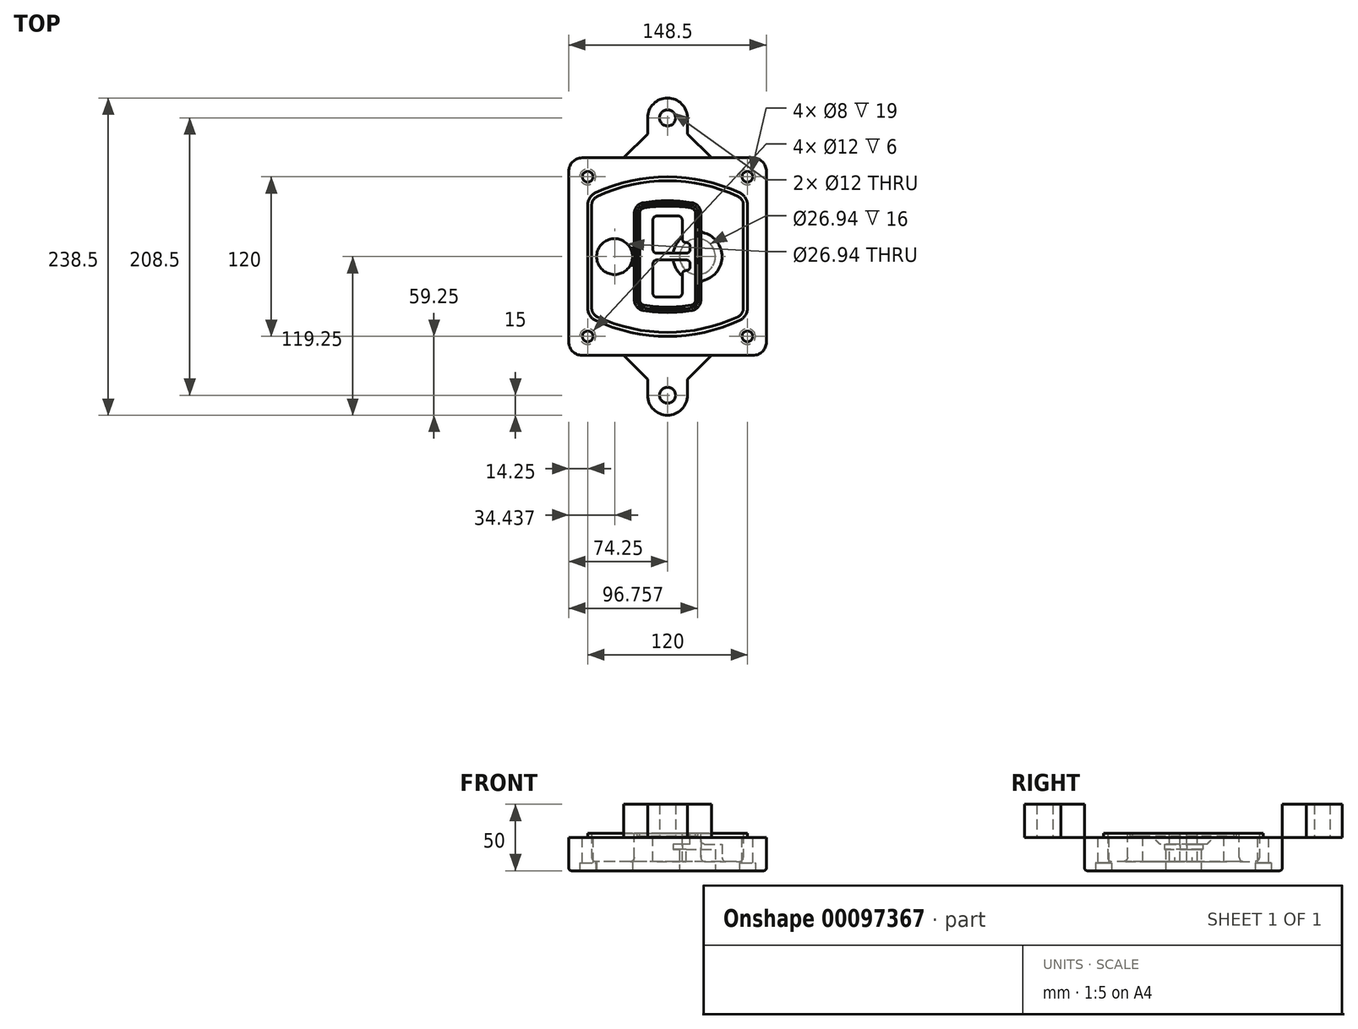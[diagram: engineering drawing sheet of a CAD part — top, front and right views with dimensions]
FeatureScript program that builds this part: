
annotation { "Feature Type Name" : "Feature", "Feature Type Description" : "" }
export const myFeature = defineFeature(function(context is Context, id is Id, definition is map)
    precondition{}
    {
        {
            var Q0;
            Q0=qCreatedBy(makeId("Top.planeOp"),FACE);
            var sketch = newSketch(context, id + "F0", { "sketchPlane" : qUnion([Q0])});
            skPoint(sketch, "E0.rect.middle", {"position": v(0, 0) * mm});
            skLineSegment(sketch, "E1.bottom", {"start": v(-64.25, -74.25) * mm, "end": v(64.25, -74.25) * mm});
            skLineSegment(sketch, "E1.top", {"start": v(-64.25, 74.25) * mm, "end": v(64.25, 74.25) * mm});
            skLineSegment(sketch, "E1.left", {"start": v(-74.25, -64.25) * mm, "end": v(-74.25, 64.25) * mm});
            skLineSegment(sketch, "E1.right", {"start": v(74.25, -64.25) * mm, "end": v(74.25, 64.25) * mm});
            skLineSegment(sketch, "E2", {"start": v(-74.25, 74.25) * mm, "end": v(74.25, -74.25) * mm, "construction": true});
            skLineSegment(sketch, "E3", {"start": v(74.25, 74.25) * mm, "end": v(-74.25, -74.25) * mm, "construction": true});
            skCircle(sketch, "E4", {"center": v(-60, 60) * mm, "radius": 4 * mm});
            skCircle(sketch, "E5", {"center": v(60, 60) * mm, "radius": 4 * mm});
            skCircle(sketch, "E6", {"center": v(60, -60) * mm, "radius": 4 * mm});
            skCircle(sketch, "E7", {"center": v(-60, -60) * mm, "radius": 4 * mm});
            skLineSegment(sketch, "E8", {"start": v(-60, 60) * mm, "end": v(60, 60) * mm, "construction": true});
            skLineSegment(sketch, "E9", {"start": v(60, 60) * mm, "end": v(60, -60) * mm, "construction": true});
            skLineSegment(sketch, "E10", {"start": v(60, -60) * mm, "end": v(-60, -60) * mm, "construction": true});
            skLineSegment(sketch, "E11", {"start": v(-60, -60) * mm, "end": v(-60, 60) * mm, "construction": true});
            skLineSegment(sketch, "E12", {"start": v(-60, 38.83) * mm, "end": v(-60, -38.83) * mm});
            skLineSegment(sketch, "E13", {"start": v(60, 38.83) * mm, "end": v(60, -38.83) * mm});
            skArc(sketch, "E14", {"start": v(54.26, 47.88) * mm, "mid": v(0, 60) * mm, "end": v(-54.26, 47.88) * mm});
            skArc(sketch, "E15", {"start": v(-54.26, -47.88) * mm, "mid": v(0, -60) * mm, "end": v(54.26, -47.88) * mm});
            skLineSegment(sketch, "E16", {"start": v(-60, 0) * mm, "end": v(60, 0) * mm, "construction": true});
            skPoint(sketch, "E17.visualSharp", {"position": v(-60, -45) * mm});
            skArc(sketch, "E17.filletArc", {"start": v(-60, -38.83) * mm, "mid": v(-58.44, -44.2) * mm, "end": v(-54.26, -47.88) * mm});
            skPoint(sketch, "E18.visualSharp", {"position": v(-60, 45) * mm});
            skArc(sketch, "E18.filletArc", {"start": v(-54.26, 47.88) * mm, "mid": v(-58.44, 44.2) * mm, "end": v(-60, 38.83) * mm});
            skPoint(sketch, "E19.visualSharp", {"position": v(60, 45) * mm});
            skArc(sketch, "E19.filletArc", {"start": v(60, 38.83) * mm, "mid": v(58.44, 44.2) * mm, "end": v(54.26, 47.88) * mm});
            skPoint(sketch, "E20.visualSharp", {"position": v(60, -45) * mm});
            skArc(sketch, "E20.filletArc", {"start": v(54.26, -47.88) * mm, "mid": v(58.44, -44.2) * mm, "end": v(60, -38.83) * mm});
            skPoint(sketch, "E21.visualSharp", {"position": v(-74.25, 74.25) * mm});
            skArc(sketch, "E21.filletArc", {"start": v(-64.25, 74.25) * mm, "mid": v(-71.32, 71.32) * mm, "end": v(-74.25, 64.25) * mm});
            skPoint(sketch, "E22.visualSharp", {"position": v(74.25, 74.25) * mm});
            skArc(sketch, "E22.filletArc", {"start": v(74.25, 64.25) * mm, "mid": v(71.32, 71.32) * mm, "end": v(64.25, 74.25) * mm});
            skPoint(sketch, "E23.visualSharp", {"position": v(74.25, -74.25) * mm});
            skArc(sketch, "E23.filletArc", {"start": v(64.25, -74.25) * mm, "mid": v(71.32, -71.32) * mm, "end": v(74.25, -64.25) * mm});
            skPoint(sketch, "E24.visualSharp", {"position": v(-74.25, -74.25) * mm});
            skArc(sketch, "E24.filletArc", {"start": v(-74.25, -64.25) * mm, "mid": v(-71.32, -71.32) * mm, "end": v(-64.25, -74.25) * mm});
            skArc(sketch, "E25.0", {"start": v(57, 38.83) * mm, "mid": v(55.9, 42.58) * mm, "end": v(52.98, 45.17) * mm});
            skLineSegment(sketch, "E25.1", {"start": v(57, 38.83) * mm, "end": v(57, -38.83) * mm});
            skArc(sketch, "E25.2", {"start": v(52.98, -45.17) * mm, "mid": v(55.9, -42.58) * mm, "end": v(57, -38.83) * mm});
            skArc(sketch, "E25.3", {"start": v(-52.98, -45.17) * mm, "mid": v(0, -57) * mm, "end": v(52.98, -45.17) * mm});
            skArc(sketch, "E25.4", {"start": v(-57, -38.83) * mm, "mid": v(-55.9, -42.58) * mm, "end": v(-52.98, -45.17) * mm});
            skArc(sketch, "E25.5", {"start": v(52.98, 45.17) * mm, "mid": v(0, 57) * mm, "end": v(-52.98, 45.17) * mm});
            skLineSegment(sketch, "E25.6", {"start": v(-57, 38.83) * mm, "end": v(-57, -38.83) * mm});
            skArc(sketch, "E25.7", {"start": v(-52.98, 45.17) * mm, "mid": v(-55.9, 42.58) * mm, "end": v(-57, 38.83) * mm});
            skArc(sketch, "E26.0", {"start": v(-55.96, 51.5) * mm, "mid": v(-61.82, 46.33) * mm, "end": v(-64, 38.83) * mm});
            skArc(sketch, "E26.1", {"start": v(55.96, 51.5) * mm, "mid": v(0, 64) * mm, "end": v(-55.96, 51.5) * mm});
            skArc(sketch, "E26.2", {"start": v(64, 38.83) * mm, "mid": v(61.82, 46.33) * mm, "end": v(55.96, 51.5) * mm});
            skLineSegment(sketch, "E26.3", {"start": v(64, 38.83) * mm, "end": v(64, -38.83) * mm});
            skArc(sketch, "E26.4", {"start": v(55.96, -51.5) * mm, "mid": v(61.82, -46.33) * mm, "end": v(64, -38.83) * mm});
            skLineSegment(sketch, "E26.5", {"start": v(-64, 38.83) * mm, "end": v(-64, -38.83) * mm});
            skArc(sketch, "E26.6", {"start": v(-55.96, -51.5) * mm, "mid": v(0, -64) * mm, "end": v(55.96, -51.5) * mm});
            skArc(sketch, "E26.7", {"start": v(-64, -38.83) * mm, "mid": v(-61.82, -46.33) * mm, "end": v(-55.96, -51.5) * mm});
            skSolve(sketch);
        }
        {
            var Q0;
            Q0=makeQuery(id+"F0.imprint","IMPRINT",FACE,{"disambiguationData":[TD([[makeQuery(id+"F0.imprint","IMPRINT",EDGE,{"derivedFrom":sQuery(id+"F0.wireOp",EDGE,"E1.bottom")}),1.0]])]});
            var Q1;
            Q1=makeQuery(id+"F0.imprint","IMPRINT",FACE,{"disambiguationData":[TD([[makeQuery(id+"F0.imprint","IMPRINT",EDGE,{"derivedFrom":sQuery(id+"F0.wireOp",EDGE,"E12")}),1.0]])]});
            var Q2;
            Q2=makeQuery(id+"F0.imprint","IMPRINT",FACE,{"disambiguationData":[TD([[makeQuery(id+"F0.imprint","IMPRINT",EDGE,{"derivedFrom":sQuery(id+"F0.wireOp",EDGE,"E25.0")}),1.0]])]});
            var Q3;
            Q3=makeQuery(id+"F0.imprint","IMPRINT",FACE,{"disambiguationData":[TD([[makeQuery(id+"F0.imprint","IMPRINT",EDGE,{"derivedFrom":sQuery(id+"F0.wireOp",EDGE,"E12")}),-1.0]])]});
            extrude(context, id + "F1", {"entities" : qUnion([Q0, Q1, Q2, Q3]), "oppositeDirection" : true, "depth" : 25 * mm});
        }
        {
            var Q0;
            Q0=makeQuery(id+"F0.imprint","IMPRINT",FACE,{"disambiguationData":[TD([[makeQuery(id+"F0.imprint","IMPRINT",EDGE,{"derivedFrom":sQuery(id+"F0.wireOp",EDGE,"E12")}),1.0]])]});
            extrude(context, id + "F2", {"entities" : qUnion([Q0]), "operationType" : NewBodyOperationType.ADD, "depth" : 3 * mm});
        }
        {
            var Q0;
            Q0=makeQuery(id+"F0.imprint","IMPRINT",FACE,{"disambiguationData":[TD([[makeQuery(id+"F0.imprint","IMPRINT",EDGE,{"derivedFrom":sQuery(id+"F0.wireOp",EDGE,"E25.0")}),1.0]])]});
            extrude(context, id + "F3", {"entities" : qUnion([Q0]), "operationType" : NewBodyOperationType.REMOVE, "oppositeDirection" : true, "depth" : 18 * mm});
        }
        {
            var Q0;
            Q0=makeQuery(id+"F2.opExtrude","CAP_FACE",FACE,{"disambiguationData":[OSD([sQuery(id+"F0.wireOp",EDGE,"E12"),sQuery(id+"F0.wireOp",EDGE,"E13"),sQuery(id+"F0.wireOp",EDGE,"E14"),sQuery(id+"F0.wireOp",EDGE,"E15"),sQuery(id+"F0.wireOp",EDGE,"E17.filletArc"),sQuery(id+"F0.wireOp",EDGE,"E18.filletArc"),sQuery(id+"F0.wireOp",EDGE,"E19.filletArc"),sQuery(id+"F0.wireOp",EDGE,"E20.filletArc"),sQuery(id+"F0.wireOp",EDGE,"E25.0"),sQuery(id+"F0.wireOp",EDGE,"E25.1"),sQuery(id+"F0.wireOp",EDGE,"E25.2"),sQuery(id+"F0.wireOp",EDGE,"E25.3"),sQuery(id+"F0.wireOp",EDGE,"E25.4"),sQuery(id+"F0.wireOp",EDGE,"E25.5"),sQuery(id+"F0.wireOp",EDGE,"E25.6"),sQuery(id+"F0.wireOp",EDGE,"E25.7")])],"isStart":false});
            var sketch = newSketch(context, id + "F4", { "sketchPlane" : qUnion([Q0])});
            skArc(sketch, "E27.0", {"start": v(-18.34, -40.45) * mm, "mid": v(0, -42) * mm, "end": v(18.34, -40.45) * mm});
            skArc(sketch, "E28.0", {"start": v(18.34, 40.45) * mm, "mid": v(0, 42) * mm, "end": v(-18.34, 40.45) * mm});
            skLineSegment(sketch, "E29", {"start": v(-25, 32.57) * mm, "end": v(-25, -32.57) * mm});
            skLineSegment(sketch, "E30", {"start": v(25, 32.57) * mm, "end": v(25, -32.57) * mm});
            skLineSegment(sketch, "E31", {"start": v(-25, 39.1) * mm, "end": v(25, 39.1) * mm, "construction": true});
            skLineSegment(sketch, "E32", {"start": v(-25, -39.1) * mm, "end": v(25, -39.1) * mm, "construction": true});
            skPoint(sketch, "E33.visualSharp", {"position": v(-25, 39.1) * mm});
            skArc(sketch, "E33.filletArc", {"start": v(-18.34, 40.45) * mm, "mid": v(-23.11, 37.73) * mm, "end": v(-25, 32.57) * mm});
            skPoint(sketch, "E34.visualSharp", {"position": v(25, 39.1) * mm});
            skArc(sketch, "E34.filletArc", {"start": v(25, 32.57) * mm, "mid": v(23.11, 37.73) * mm, "end": v(18.34, 40.45) * mm});
            skPoint(sketch, "E35.visualSharp", {"position": v(25, -39.1) * mm});
            skArc(sketch, "E35.filletArc", {"start": v(18.34, -40.45) * mm, "mid": v(23.11, -37.73) * mm, "end": v(25, -32.57) * mm});
            skPoint(sketch, "E36.visualSharp", {"position": v(-25, -39.1) * mm});
            skArc(sketch, "E36.filletArc", {"start": v(-25, -32.57) * mm, "mid": v(-23.11, -37.73) * mm, "end": v(-18.34, -40.45) * mm});
            skArc(sketch, "E37.0", {"start": v(52.98, 45.17) * mm, "mid": v(0, 57) * mm, "end": v(-52.98, 45.17) * mm});
            skArc(sketch, "E37.1", {"start": v(-52.98, 45.17) * mm, "mid": v(-55.9, 42.58) * mm, "end": v(-57, 38.83) * mm});
            skLineSegment(sketch, "E37.2", {"start": v(-57, 38.83) * mm, "end": v(-57, -38.83) * mm});
            skArc(sketch, "E37.3", {"start": v(-57, -38.83) * mm, "mid": v(-55.9, -42.58) * mm, "end": v(-52.98, -45.17) * mm});
            skArc(sketch, "E37.4", {"start": v(-52.98, -45.17) * mm, "mid": v(0, -57) * mm, "end": v(52.98, -45.17) * mm});
            skArc(sketch, "E37.5", {"start": v(52.98, -45.17) * mm, "mid": v(55.9, -42.58) * mm, "end": v(57, -38.83) * mm});
            skLineSegment(sketch, "E37.6", {"start": v(57, 38.83) * mm, "end": v(57, -38.83) * mm});
            skArc(sketch, "E37.7", {"start": v(57, 38.83) * mm, "mid": v(55.9, 42.58) * mm, "end": v(52.98, 45.17) * mm});
            skLineSegment(sketch, "E38.0", {"start": v(23, 32.57) * mm, "end": v(23, -32.57) * mm});
            skArc(sketch, "E38.1", {"start": v(18, -38.48) * mm, "mid": v(21.58, -36.44) * mm, "end": v(23, -32.57) * mm});
            skArc(sketch, "E38.2", {"start": v(-18, -38.48) * mm, "mid": v(0, -40) * mm, "end": v(18, -38.48) * mm});
            skArc(sketch, "E38.3", {"start": v(-23, -32.57) * mm, "mid": v(-21.58, -36.44) * mm, "end": v(-18, -38.48) * mm});
            skLineSegment(sketch, "E38.4", {"start": v(-23, 32.57) * mm, "end": v(-23, -32.57) * mm});
            skArc(sketch, "E38.5", {"start": v(23, 32.57) * mm, "mid": v(21.58, 36.44) * mm, "end": v(18, 38.48) * mm});
            skArc(sketch, "E38.6", {"start": v(-18, 38.48) * mm, "mid": v(-21.58, 36.44) * mm, "end": v(-23, 32.57) * mm});
            skArc(sketch, "E38.7", {"start": v(18, 38.48) * mm, "mid": v(0, 40) * mm, "end": v(-18, 38.48) * mm});
            skArc(sketch, "E39.0", {"start": v(21, 32.57) * mm, "mid": v(20.06, 35.15) * mm, "end": v(17.67, 36.5) * mm});
            skLineSegment(sketch, "E39.1", {"start": v(21, 32.57) * mm, "end": v(21, -32.57) * mm});
            skArc(sketch, "E39.2", {"start": v(17.67, -36.5) * mm, "mid": v(20.06, -35.15) * mm, "end": v(21, -32.57) * mm});
            skArc(sketch, "E39.3", {"start": v(-17.67, -36.5) * mm, "mid": v(0, -38) * mm, "end": v(17.67, -36.5) * mm});
            skArc(sketch, "E39.4", {"start": v(-21, -32.57) * mm, "mid": v(-20.06, -35.15) * mm, "end": v(-17.67, -36.5) * mm});
            skArc(sketch, "E39.5", {"start": v(17.67, 36.5) * mm, "mid": v(0, 38) * mm, "end": v(-17.67, 36.5) * mm});
            skLineSegment(sketch, "E39.6", {"start": v(-21, 32.57) * mm, "end": v(-21, -32.57) * mm});
            skArc(sketch, "E39.7", {"start": v(-17.67, 36.5) * mm, "mid": v(-20.06, 35.15) * mm, "end": v(-21, 32.57) * mm});
            skLineSegment(sketch, "E40", {"start": v(-25, 0) * mm, "end": v(25, 0) * mm, "construction": true});
            skLineSegment(sketch, "E41", {"start": v(-11, 5.5) * mm, "end": v(-11, 27.5) * mm});
            skLineSegment(sketch, "E42", {"start": v(-8, 30.5) * mm, "end": v(8, 30.5) * mm});
            skLineSegment(sketch, "E43", {"start": v(11, 27.5) * mm, "end": v(11, 13.5) * mm});
            skLineSegment(sketch, "E44", {"start": v(14, 10.5) * mm, "end": v(14, 10.5) * mm});
            skLineSegment(sketch, "E45", {"start": v(17, 7.5) * mm, "end": v(17, 5.5) * mm});
            skLineSegment(sketch, "E46", {"start": v(14, 2.5) * mm, "end": v(-8, 2.5) * mm});
            skPoint(sketch, "E47.visualSharp", {"position": v(-11, 30.5) * mm});
            skArc(sketch, "E47.filletArc", {"start": v(-8, 30.5) * mm, "mid": v(-10.12, 29.62) * mm, "end": v(-11, 27.5) * mm});
            skPoint(sketch, "E48.visualSharp", {"position": v(11, 30.5) * mm});
            skArc(sketch, "E48.filletArc", {"start": v(11, 27.5) * mm, "mid": v(10.12, 29.62) * mm, "end": v(8, 30.5) * mm});
            skPoint(sketch, "E49.visualSharp", {"position": v(11, 10.5) * mm});
            skArc(sketch, "E49.filletArc", {"start": v(11, 13.5) * mm, "mid": v(11.88, 11.38) * mm, "end": v(14, 10.5) * mm});
            skPoint(sketch, "E50.visualSharp", {"position": v(17, 10.5) * mm});
            skArc(sketch, "E50.filletArc", {"start": v(17, 7.5) * mm, "mid": v(16.12, 9.62) * mm, "end": v(14, 10.5) * mm});
            skPoint(sketch, "E51.visualSharp", {"position": v(17, 2.5) * mm});
            skArc(sketch, "E51.filletArc", {"start": v(14, 2.5) * mm, "mid": v(16.12, 3.38) * mm, "end": v(17, 5.5) * mm});
            skPoint(sketch, "E52.visualSharp", {"position": v(-11, 2.5) * mm});
            skArc(sketch, "E52.filletArc", {"start": v(-11, 5.5) * mm, "mid": v(-10.12, 3.38) * mm, "end": v(-8, 2.5) * mm});
            skLineSegment(sketch, "E53.0.MirrorCS", {"start": v(14, -2.5) * mm, "end": v(-8, -2.5) * mm});
            skArc(sketch, "E54.0.MirrorCS", {"start": v(-11, -5.5) * mm, "mid": v(-10.12, -3.38) * mm, "end": v(-8, -2.5) * mm});
            skLineSegment(sketch, "E55.0.MirrorCS", {"start": v(-11, -5.5) * mm, "end": v(-11, -27.5) * mm});
            skArc(sketch, "E56.0.MirrorCS", {"start": v(-8, -30.5) * mm, "mid": v(-10.12, -29.62) * mm, "end": v(-11, -27.5) * mm});
            skLineSegment(sketch, "E57.0.MirrorCS", {"start": v(-8, -30.5) * mm, "end": v(8, -30.5) * mm});
            skArc(sketch, "E58.0.MirrorCS", {"start": v(11, -27.5) * mm, "mid": v(10.12, -29.62) * mm, "end": v(8, -30.5) * mm});
            skLineSegment(sketch, "E59.0.MirrorCS", {"start": v(11, -27.5) * mm, "end": v(11, -13.5) * mm});
            skArc(sketch, "E60.0.MirrorCS", {"start": v(11, -13.5) * mm, "mid": v(11.88, -11.38) * mm, "end": v(14, -10.5) * mm});
            skArc(sketch, "E61.0.MirrorCS", {"start": v(17, -7.5) * mm, "mid": v(16.12, -9.62) * mm, "end": v(14, -10.5) * mm});
            skLineSegment(sketch, "E62.0.MirrorCS", {"start": v(17, -7.5) * mm, "end": v(17, -5.5) * mm});
            skArc(sketch, "E63.0.MirrorCS", {"start": v(14, -2.5) * mm, "mid": v(16.12, -3.38) * mm, "end": v(17, -5.5) * mm});
            skSolve(sketch);
        }
        {
            var Q0;
            Q0=makeQuery(id+"F4.imprint","IMPRINT",FACE,{"disambiguationData":[TD([[makeQuery(id+"F4.imprint","IMPRINT",EDGE,{"derivedFrom":sQuery(id+"F4.wireOp",EDGE,"E27.0")}),1.0]])]});
            var Q1;
            Q1=makeQuery(id+"F4.imprint","IMPRINT",FACE,{"disambiguationData":[TD([[makeQuery(id+"F4.imprint","IMPRINT",EDGE,{"derivedFrom":sQuery(id+"F4.wireOp",EDGE,"E38.0")}),-1.0]])]});
            var Q2;
            Q2=makeQuery(id+"F4.imprint","IMPRINT",FACE,{"disambiguationData":[TD([[makeQuery(id+"F4.imprint","IMPRINT",EDGE,{"derivedFrom":sQuery(id+"F4.wireOp",EDGE,"E39.0")}),1.0]])]});
            extrude(context, id + "F5", {"entities" : qUnion([Q0, Q1, Q2]), "operationType" : NewBodyOperationType.ADD, "endBound" : BoundingType.UP_TO_NEXT, "oppositeDirection" : true, "depth" : 25 * mm});
        }
        {
            var Q0;
            Q0=makeQuery(id+"F4.imprint","IMPRINT",FACE,{"disambiguationData":[TD([[makeQuery(id+"F4.imprint","IMPRINT",EDGE,{"derivedFrom":sQuery(id+"F4.wireOp",EDGE,"E38.0")}),-1.0]])]});
            extrude(context, id + "F6", {"entities" : qUnion([Q0]), "operationType" : NewBodyOperationType.REMOVE, "oppositeDirection" : true, "depth" : 2 * mm});
        }
        {
            var Q0;
            Q0=makeQuery(id+"F1.opExtrude","CAP_FACE",FACE,{"disambiguationData":[OSD([sQuery(id+"F0.wireOp",EDGE,"E1.bottom"),sQuery(id+"F0.wireOp",EDGE,"E1.top"),sQuery(id+"F0.wireOp",EDGE,"E1.left"),sQuery(id+"F0.wireOp",EDGE,"E1.right"),sQuery(id+"F0.wireOp",EDGE,"E4"),sQuery(id+"F0.wireOp",EDGE,"E5"),sQuery(id+"F0.wireOp",EDGE,"E6"),sQuery(id+"F0.wireOp",EDGE,"E7"),sQuery(id+"F0.wireOp",EDGE,"E21.filletArc"),sQuery(id+"F0.wireOp",EDGE,"E22.filletArc"),sQuery(id+"F0.wireOp",EDGE,"E23.filletArc"),sQuery(id+"F0.wireOp",EDGE,"E24.filletArc")])],"isStart":false});
            var sketch = newSketch(context, id + "F7", { "sketchPlane" : qUnion([Q0])});
            skCircle(sketch, "E64", {"center": v(22.5, 0) * mm, "radius": 13.47 * mm});
            skCircle(sketch, "E65", {"center": v(-39.81, 0) * mm, "radius": 13.47 * mm});
            skLineSegment(sketch, "E66", {"start": v(74.25, 0) * mm, "end": v(-74.25, 0) * mm});
            skCircle(sketch, "E67", {"center": v(22.5, 0) * mm, "radius": 18.47 * mm});
            skCircle(sketch, "E68", {"center": v(60, -60) * mm, "radius": 6 * mm});
            skCircle(sketch, "E69", {"center": v(-60, -60) * mm, "radius": 6 * mm});
            skCircle(sketch, "E70", {"center": v(-60, 60) * mm, "radius": 6 * mm});
            skCircle(sketch, "E71", {"center": v(60, 60) * mm, "radius": 6 * mm});
            skSolve(sketch);
        }
        {
            var Q0;
            {var subQ1=sQuery(id+"F7.wireOp",EDGE,"E66");var subQ4=sQuery(id+"F7.wireOp",EDGE,"E64");var subQ6=makeQuery(id+"F7.imprint","INTERSECT",VERTEX,{"disambiguationData":[OD(0.0)],"derivedFrom":[subQ4,subQ1]});Q0=makeQuery(id+"F7.imprint","IMPRINT",FACE,{"disambiguationData":[TD([[makeQuery(id+"F7.imprint","IMPRINT",EDGE,{"disambiguationData":[TD([[subQ6,-1.0]])],"derivedFrom":subQ4}),-1.0]])]});}
            var Q1;
            {var subQ0=sQuery(id+"F7.wireOp",EDGE,"E66");var subQ1=sQuery(id+"F7.wireOp",EDGE,"E64");var subQ3=makeQuery(id+"F7.imprint","INTERSECT",VERTEX,{"disambiguationData":[OD(0.0)],"derivedFrom":[subQ1,subQ0]});Q1=makeQuery(id+"F7.imprint","IMPRINT",FACE,{"disambiguationData":[TD([[makeQuery(id+"F7.imprint","IMPRINT",EDGE,{"disambiguationData":[TD([[subQ3,-1.0]])],"derivedFrom":subQ1}),1.0]])]});}
            var Q2;
            {var subQ0=sQuery(id+"F7.wireOp",EDGE,"E66");var subQ1=sQuery(id+"F7.wireOp",EDGE,"E64");var subQ3=makeQuery(id+"F7.imprint","INTERSECT",VERTEX,{"disambiguationData":[OD(0.0)],"derivedFrom":[subQ1,subQ0]});Q2=makeQuery(id+"F7.imprint","IMPRINT",FACE,{"disambiguationData":[TD([[makeQuery(id+"F7.imprint","IMPRINT",EDGE,{"disambiguationData":[TD([[subQ3,1.0]])],"derivedFrom":subQ1}),1.0]])]});}
            var Q3;
            {var subQ1=sQuery(id+"F7.wireOp",EDGE,"E66");var subQ4=sQuery(id+"F7.wireOp",EDGE,"E64");var subQ6=makeQuery(id+"F7.imprint","INTERSECT",VERTEX,{"disambiguationData":[OD(0.0)],"derivedFrom":[subQ4,subQ1]});Q3=makeQuery(id+"F7.imprint","IMPRINT",FACE,{"disambiguationData":[TD([[makeQuery(id+"F7.imprint","IMPRINT",EDGE,{"disambiguationData":[TD([[subQ6,1.0]])],"derivedFrom":subQ4}),-1.0]])]});}
            extrude(context, id + "F8", {"entities" : qUnion([Q0, Q1, Q2, Q3]), "operationType" : NewBodyOperationType.ADD, "oppositeDirection" : true, "depth" : 20 * mm});
        }
        {
            var Q0;
            {var subQ0=sQuery(id+"F7.wireOp",EDGE,"E66");var subQ1=sQuery(id+"F7.wireOp",EDGE,"E64");var subQ3=makeQuery(id+"F7.imprint","INTERSECT",VERTEX,{"disambiguationData":[OD(0.0)],"derivedFrom":[subQ1,subQ0]});Q0=makeQuery(id+"F7.imprint","IMPRINT",FACE,{"disambiguationData":[TD([[makeQuery(id+"F7.imprint","IMPRINT",EDGE,{"disambiguationData":[TD([[subQ3,-1.0]])],"derivedFrom":subQ1}),1.0]])]});}
            var Q1;
            {var subQ0=sQuery(id+"F7.wireOp",EDGE,"E66");var subQ1=sQuery(id+"F7.wireOp",EDGE,"E64");var subQ3=makeQuery(id+"F7.imprint","INTERSECT",VERTEX,{"disambiguationData":[OD(0.0)],"derivedFrom":[subQ1,subQ0]});Q1=makeQuery(id+"F7.imprint","IMPRINT",FACE,{"disambiguationData":[TD([[makeQuery(id+"F7.imprint","IMPRINT",EDGE,{"disambiguationData":[TD([[subQ3,1.0]])],"derivedFrom":subQ1}),1.0]])]});}
            extrude(context, id + "F9", {"entities" : qUnion([Q0, Q1]), "operationType" : NewBodyOperationType.REMOVE, "oppositeDirection" : true, "depth" : 16 * mm});
        }
        {
            var Q0;
            {var subQ0=sQuery(id+"F7.wireOp",EDGE,"E66");var subQ1=sQuery(id+"F7.wireOp",EDGE,"E65");var subQ3=makeQuery(id+"F7.imprint","INTERSECT",VERTEX,{"disambiguationData":[OD(0.0)],"derivedFrom":[subQ1,subQ0]});Q0=makeQuery(id+"F7.imprint","IMPRINT",FACE,{"disambiguationData":[TD([[makeQuery(id+"F7.imprint","IMPRINT",EDGE,{"disambiguationData":[TD([[subQ3,-1.0]])],"derivedFrom":subQ1}),1.0]])]});}
            var Q1;
            {var subQ0=sQuery(id+"F7.wireOp",EDGE,"E66");var subQ1=sQuery(id+"F7.wireOp",EDGE,"E65");var subQ3=makeQuery(id+"F7.imprint","INTERSECT",VERTEX,{"disambiguationData":[OD(0.0)],"derivedFrom":[subQ1,subQ0]});Q1=makeQuery(id+"F7.imprint","IMPRINT",FACE,{"disambiguationData":[TD([[makeQuery(id+"F7.imprint","IMPRINT",EDGE,{"disambiguationData":[TD([[subQ3,1.0]])],"derivedFrom":subQ1}),1.0]])]});}
            extrude(context, id + "F10", {"entities" : qUnion([Q0, Q1]), "operationType" : NewBodyOperationType.REMOVE, "oppositeDirection" : true, "depth" : 25 * mm});
        }
        {
            var Q0;
            Q0=makeQuery(id+"F7.imprint","IMPRINT",FACE,{"disambiguationData":[TD([[makeQuery(id+"F7.imprint","IMPRINT",EDGE,{"derivedFrom":sQuery(id+"F7.wireOp",EDGE,"E68")}),1.0]])]});
            var Q1;
            Q1=makeQuery(id+"F7.imprint","IMPRINT",FACE,{"disambiguationData":[TD([[makeQuery(id+"F7.imprint","IMPRINT",EDGE,{"derivedFrom":makeQuery(id+"F1.opExtrude","CAP_EDGE",EDGE,{"disambiguationData":[OSD([sQuery(id+"F0.wireOp",EDGE,"E5")])],"isStart":false})}),-1.0]])]});
            var Q2;
            Q2=makeQuery(id+"F7.imprint","IMPRINT",FACE,{"disambiguationData":[TD([[makeQuery(id+"F7.imprint","IMPRINT",EDGE,{"derivedFrom":sQuery(id+"F7.wireOp",EDGE,"E69")}),1.0]])]});
            var Q3;
            Q3=makeQuery(id+"F7.imprint","IMPRINT",FACE,{"disambiguationData":[TD([[makeQuery(id+"F7.imprint","IMPRINT",EDGE,{"derivedFrom":makeQuery(id+"F1.opExtrude","CAP_EDGE",EDGE,{"disambiguationData":[OSD([sQuery(id+"F0.wireOp",EDGE,"E4")])],"isStart":false})}),-1.0]])]});
            var Q4;
            Q4=makeQuery(id+"F7.imprint","IMPRINT",FACE,{"disambiguationData":[TD([[makeQuery(id+"F7.imprint","IMPRINT",EDGE,{"derivedFrom":sQuery(id+"F7.wireOp",EDGE,"E70")}),1.0]])]});
            var Q5;
            Q5=makeQuery(id+"F7.imprint","IMPRINT",FACE,{"disambiguationData":[TD([[makeQuery(id+"F7.imprint","IMPRINT",EDGE,{"derivedFrom":makeQuery(id+"F1.opExtrude","CAP_EDGE",EDGE,{"disambiguationData":[OSD([sQuery(id+"F0.wireOp",EDGE,"E7")])],"isStart":false})}),-1.0]])]});
            var Q6;
            Q6=makeQuery(id+"F7.imprint","IMPRINT",FACE,{"disambiguationData":[TD([[makeQuery(id+"F7.imprint","IMPRINT",EDGE,{"derivedFrom":sQuery(id+"F7.wireOp",EDGE,"E71")}),1.0]])]});
            var Q7;
            Q7=makeQuery(id+"F7.imprint","IMPRINT",FACE,{"disambiguationData":[TD([[makeQuery(id+"F7.imprint","IMPRINT",EDGE,{"derivedFrom":makeQuery(id+"F1.opExtrude","CAP_EDGE",EDGE,{"disambiguationData":[OSD([sQuery(id+"F0.wireOp",EDGE,"E6")])],"isStart":false})}),-1.0]])]});
            extrude(context, id + "F11", {"entities" : qUnion([Q0, Q1, Q2, Q3, Q4, Q5, Q6, Q7]), "operationType" : NewBodyOperationType.REMOVE, "oppositeDirection" : true, "depth" : 6 * mm});
        }
        {
            var Q0;
            Q0=makeQuery(id+"F9.boolean.opBoolean","COPY",FACE,{"derivedFrom":makeQuery(id+"F9.opExtrude","CAP_FACE",FACE,{"disambiguationData":[OSD([sQuery(id+"F7.wireOp",EDGE,"E64")])],"isStart":false})});
            var sketch = newSketch(context, id + "F12", { "sketchPlane" : qUnion([Q0])});
            skArc(sketch, "E72.0", {"start": v(11, 14.45) * mm, "mid": v(6.45, 9.13) * mm, "end": v(4.2, 2.5) * mm});
            skArc(sketch, "E72.1", {"start": v(4.2, -2.5) * mm, "mid": v(6.45, -9.13) * mm, "end": v(11, -14.45) * mm});
            skLineSegment(sketch, "E73", {"start": v(4.2, -2.5) * mm, "end": v(14, -2.5) * mm});
            skLineSegment(sketch, "E74.0", {"start": v(14, 2.5) * mm, "end": v(4.2, 2.5) * mm});
            skArc(sketch, "E74.1", {"start": v(14, 2.5) * mm, "mid": v(16.12, 3.38) * mm, "end": v(17, 5.5) * mm});
            skLineSegment(sketch, "E74.2", {"start": v(17, 7.5) * mm, "end": v(17, 5.5) * mm});
            skArc(sketch, "E74.3", {"start": v(17, 7.5) * mm, "mid": v(16.12, 9.62) * mm, "end": v(14, 10.5) * mm});
            skArc(sketch, "E74.4", {"start": v(11, 13.5) * mm, "mid": v(11.88, 11.38) * mm, "end": v(14, 10.5) * mm});
            skLineSegment(sketch, "E74.5", {"start": v(11, 14.45) * mm, "end": v(11, 13.5) * mm});
            skLineSegment(sketch, "E74.7", {"start": v(14, -2.5) * mm, "end": v(4.2, -2.5) * mm});
            skArc(sketch, "E74.8", {"start": v(14, -2.5) * mm, "mid": v(16.12, -3.38) * mm, "end": v(17, -5.5) * mm});
            skLineSegment(sketch, "E74.9", {"start": v(17, -7.5) * mm, "end": v(17, -5.5) * mm});
            skArc(sketch, "E74.10", {"start": v(17, -7.5) * mm, "mid": v(16.12, -9.62) * mm, "end": v(14, -10.5) * mm});
            skArc(sketch, "E74.11", {"start": v(11, -13.5) * mm, "mid": v(11.88, -11.38) * mm, "end": v(14, -10.5) * mm});
            skLineSegment(sketch, "E74.12", {"start": v(11, -14.45) * mm, "end": v(11, -13.5) * mm});
            skPoint(sketch, "E75.orphan", {"position": v(11, -27.5) * mm});
            skPoint(sketch, "E76.orphan", {"position": v(-8, -2.5) * mm});
            skPoint(sketch, "E77.orphan", {"position": v(-8, 2.5) * mm});
            skPoint(sketch, "E78.orphan", {"position": v(11, 27.5) * mm});
            skSolve(sketch);
        }
        {
            var Q0;
            {var subQ7=sQuery(id+"F12.wireOp",EDGE,"E72.0");var subQ14=sQuery(id+"F12.wireOp",EDGE,"E72.1");var subQ16=sQuery(id+"F12.wireOp",EDGE,"E74.1");var subQ18=sQuery(id+"F12.wireOp",EDGE,"E74.8");Q0=qUnion([makeQuery(id+"F12.imprint","IMPRINT",FACE,{"disambiguationData":[TD([[makeQuery(id+"F12.imprint","IMPRINT",EDGE,{"derivedFrom":subQ7}),1.0]])]}),makeQuery(id+"F12.imprint","IMPRINT",FACE,{"disambiguationData":[TD([[makeQuery(id+"F12.imprint","IMPRINT",EDGE,{"derivedFrom":subQ14}),1.0]])]}),makeQuery(id+"F12.imprint","IMPRINT",FACE,{"disambiguationData":[TD([[makeQuery(id+"F12.imprint","IMPRINT",EDGE,{"derivedFrom":subQ16}),1.0]])]}),makeQuery(id+"F12.imprint","IMPRINT",FACE,{"disambiguationData":[TD([[makeQuery(id+"F12.imprint","IMPRINT",EDGE,{"derivedFrom":subQ18}),-1.0]])]})]);}
            var Q1;
            Q1=makeQuery(id+"F5.boolean.opBoolean","SPLIT",FACE,{"disambiguationData":[TD([makeQuery(id+"F5.opExtrude","SWEPT_FACE",FACE,{"disambiguationData":[OSD([sQuery(id+"F4.wireOp",EDGE,"E41")])]})])],"derivedFrom":makeQuery(id+"F3.boolean.opBoolean","COPY",FACE,{"derivedFrom":makeQuery(id+"F3.opExtrude","CAP_FACE",FACE,{"disambiguationData":[OSD([sQuery(id+"F0.wireOp",EDGE,"E25.0"),sQuery(id+"F0.wireOp",EDGE,"E25.1"),sQuery(id+"F0.wireOp",EDGE,"E25.2"),sQuery(id+"F0.wireOp",EDGE,"E25.3"),sQuery(id+"F0.wireOp",EDGE,"E25.4"),sQuery(id+"F0.wireOp",EDGE,"E25.5"),sQuery(id+"F0.wireOp",EDGE,"E25.6"),sQuery(id+"F0.wireOp",EDGE,"E25.7")])],"isStart":false})})});
            extrude(context, id + "F13", {"entities" : qUnion([Q0]), "operationType" : NewBodyOperationType.REMOVE, "endBound" : BoundingType.UP_TO_SURFACE, "endBoundEntityFace" : qUnion([Q1]), "depth" : 25 * mm});
        }
        {
            var Q0;
            Q0=makeQuery(id+"F3.boolean.opBoolean","COPY",EDGE,{"derivedFrom":makeQuery(id+"F3.opExtrude","CAP_EDGE",EDGE,{"disambiguationData":[OSD([sQuery(id+"F0.wireOp",EDGE,"E25.6")])],"isStart":false})});
            var Q1;
            Q1=makeQuery(id+"F8.boolean.opBoolean","INTERSECT",EDGE,{"derivedFrom":[makeQuery(id+"F5.opExtrude","SWEPT_FACE",FACE,{"disambiguationData":[OSD([sQuery(id+"F4.wireOp",EDGE,"E30")])]}),makeQuery(id+"F8.opExtrude","CAP_FACE",FACE,{"disambiguationData":[OSD([sQuery(id+"F7.wireOp",EDGE,"E67")])],"isStart":false})]});
            var Q2;
            Q2=makeQuery(id+"F8.boolean.opBoolean","INTERSECT",EDGE,{"disambiguationData":[OD(1.0)],"derivedFrom":[makeQuery(id+"F5.opExtrude","SWEPT_FACE",FACE,{"disambiguationData":[OSD([sQuery(id+"F4.wireOp",EDGE,"E30")])]}),makeQuery(id+"F8.opExtrude","SWEPT_FACE",FACE,{"disambiguationData":[OSD([sQuery(id+"F7.wireOp",EDGE,"E67")])]})]});
            var Q3;
            {var subQ0=sQuery(id+"F4.wireOp",EDGE,"E30");Q3=makeQuery(id+"F8.boolean.opBoolean","SPLIT",EDGE,{"disambiguationData":[TD([makeQuery(id+"F5.opExtrude","SWEPT_FACE",FACE,{"disambiguationData":[OSD([sQuery(id+"F4.wireOp",EDGE,"E35.filletArc")])]})])],"derivedFrom":makeQuery(id+"F5.opExtrude","CAP_EDGE",EDGE,{"disambiguationData":[OSD([subQ0])],"isStart":false})});}
            var Q4;
            {var subQ0=sQuery(id+"F0.wireOp",EDGE,"E25.7");var subQ1=sQuery(id+"F0.wireOp",EDGE,"E25.1");var subQ2=sQuery(id+"F0.wireOp",EDGE,"E25.6");var subQ3=sQuery(id+"F0.wireOp",EDGE,"E25.5");var subQ4=sQuery(id+"F0.wireOp",EDGE,"E25.4");var subQ5=sQuery(id+"F0.wireOp",EDGE,"E25.0");var subQ6=sQuery(id+"F0.wireOp",EDGE,"E25.2");var subQ7=sQuery(id+"F0.wireOp",EDGE,"E25.3");Q4=makeQuery(id+"F8.boolean.opBoolean","INTERSECT",EDGE,{"derivedFrom":[makeQuery(id+"F5.boolean.opBoolean","SPLIT",FACE,{"disambiguationData":[TD([makeQuery(id+"F2.opExtrude","SWEPT_FACE",FACE,{"disambiguationData":[OSD([subQ5])]})])],"derivedFrom":makeQuery(id+"F3.boolean.opBoolean","COPY",FACE,{"derivedFrom":makeQuery(id+"F3.opExtrude","CAP_FACE",FACE,{"disambiguationData":[OSD([subQ5,subQ1,subQ6,subQ7,subQ4,subQ3,subQ2,subQ0])],"isStart":false})})}),makeQuery(id+"F8.opExtrude","SWEPT_FACE",FACE,{"disambiguationData":[OSD([sQuery(id+"F7.wireOp",EDGE,"E67")])]})]});}
            var Q5;
            Q5=makeQuery(id+"F8.boolean.opBoolean","INTERSECT",EDGE,{"disambiguationData":[OD(0.0)],"derivedFrom":[makeQuery(id+"F5.opExtrude","SWEPT_FACE",FACE,{"disambiguationData":[OSD([sQuery(id+"F4.wireOp",EDGE,"E30")])]}),makeQuery(id+"F8.opExtrude","SWEPT_FACE",FACE,{"disambiguationData":[OSD([sQuery(id+"F7.wireOp",EDGE,"E67")])]})]});
            fillet(context, id + "F14", {"entities" : qUnion([Q0, Q1, Q2, Q3, Q4, Q5]), "radius" : 3 * mm, "tangentPropagation" : true, "allowEdgeOverflow" : false});
        }
        {
            var Q0;
            Q0=makeQuery(id+"F1.opExtrude","CAP_EDGE",EDGE,{"disambiguationData":[OSD([sQuery(id+"F0.wireOp",EDGE,"E1.bottom")])],"isStart":false});
            fillet(context, id + "F15", {"entities" : qUnion([Q0]), "radius" : 2 * mm, "tangentPropagation" : true, "allowEdgeOverflow" : false});
        }
        {
            var Q0;
            {var subQ0=sQuery(id+"F0.wireOp",EDGE,"E22.filletArc");var subQ1=sQuery(id+"F0.wireOp",EDGE,"E7");var subQ2=sQuery(id+"F0.wireOp",EDGE,"E6");var subQ3=sQuery(id+"F0.wireOp",EDGE,"E5");var subQ4=sQuery(id+"F0.wireOp",EDGE,"E4");var subQ5=sQuery(id+"F0.wireOp",EDGE,"E1.bottom");var subQ6=sQuery(id+"F0.wireOp",EDGE,"E21.filletArc");var subQ7=sQuery(id+"F0.wireOp",EDGE,"E1.top");var subQ8=sQuery(id+"F0.wireOp",EDGE,"E1.left");var subQ9=sQuery(id+"F0.wireOp",EDGE,"E1.right");var subQ10=sQuery(id+"F0.wireOp",EDGE,"E23.filletArc");var subQ11=sQuery(id+"F0.wireOp",EDGE,"E24.filletArc");Q0=makeQuery(id+"F2.boolean.opBoolean","SPLIT",FACE,{"disambiguationData":[TD([makeQuery(id+"F1.opExtrude","SWEPT_FACE",FACE,{"disambiguationData":[OSD([subQ5])]})])],"derivedFrom":makeQuery(id+"F1.opExtrude","CAP_FACE",FACE,{"disambiguationData":[OSD([subQ5,subQ7,subQ8,subQ9,subQ4,subQ3,subQ2,subQ1,subQ6,subQ0,subQ10,subQ11])],"isStart":true})});}
            var sketch = newSketch(context, id + "F16", { "sketchPlane" : qUnion([Q0])});
            skLineSegment(sketch, "E79", {"start": v(0, -74.25) * mm, "end": v(0, 104.25) * mm, "construction": true});
            skPoint(sketch, "E79.endSnap0", {"position": v(0, 74.25) * mm});
            skCircle(sketch, "E80", {"center": v(0, 104.25) * mm, "radius": 6 * mm});
            skArc(sketch, "E81", {"start": v(15, 104.25) * mm, "mid": v(0, 119.25) * mm, "end": v(-15, 104.25) * mm});
            skLineSegment(sketch, "E82", {"start": v(-15, 104.25) * mm, "end": v(-15, 92.25) * mm});
            skLineSegment(sketch, "E83", {"start": v(-15, 92.25) * mm, "end": v(-33, 74.25) * mm});
            skLineSegment(sketch, "E84", {"start": v(15, 104.25) * mm, "end": v(15, 92.25) * mm});
            skLineSegment(sketch, "E85", {"start": v(15, 92.25) * mm, "end": v(33, 74.25) * mm});
            skLineSegment(sketch, "E86", {"start": v(-74.25, 0) * mm, "end": v(74.25, 0) * mm, "construction": true});
            skLineSegment(sketch, "E87.MirrorCS", {"start": v(15, -92.25) * mm, "end": v(33, -74.25) * mm});
            skLineSegment(sketch, "E88.MirrorCS", {"start": v(15, -104.25) * mm, "end": v(15, -92.25) * mm});
            skArc(sketch, "E89.MirrorCS", {"start": v(15, -104.25) * mm, "mid": v(0, -119.25) * mm, "end": v(-15, -104.25) * mm});
            skCircle(sketch, "E90.MirrorC", {"center": v(0, -104.25) * mm, "radius": 6 * mm});
            skLineSegment(sketch, "E91.MirrorCS", {"start": v(-15, -104.25) * mm, "end": v(-15, -92.25) * mm});
            skLineSegment(sketch, "E92.MirrorCS", {"start": v(-15, -92.25) * mm, "end": v(-33, -74.25) * mm});
            skSolve(sketch);
        }
        {
            var Q0;
            Q0=makeQuery(id+"F16.imprint","IMPRINT",FACE,{"disambiguationData":[TD([[makeQuery(id+"F16.imprint","IMPRINT",EDGE,{"derivedFrom":sQuery(id+"F16.wireOp",EDGE,"E80")}),-1.0]])]});
            var Q1;
            {var subQ0=sQuery(id+"F16.wireOp",EDGE,"E87.MirrorCS");Q1=makeQuery(id+"F16.imprint","IMPRINT",FACE,{"disambiguationData":[TD([[makeQuery(id+"F16.imprint","IMPRINT",EDGE,{"derivedFrom":subQ0}),1.0]])]});}
            extrude(context, id + "F17", {"entities" : qUnion([Q0, Q1]), "depth" : 25 * mm});
        }
    });
